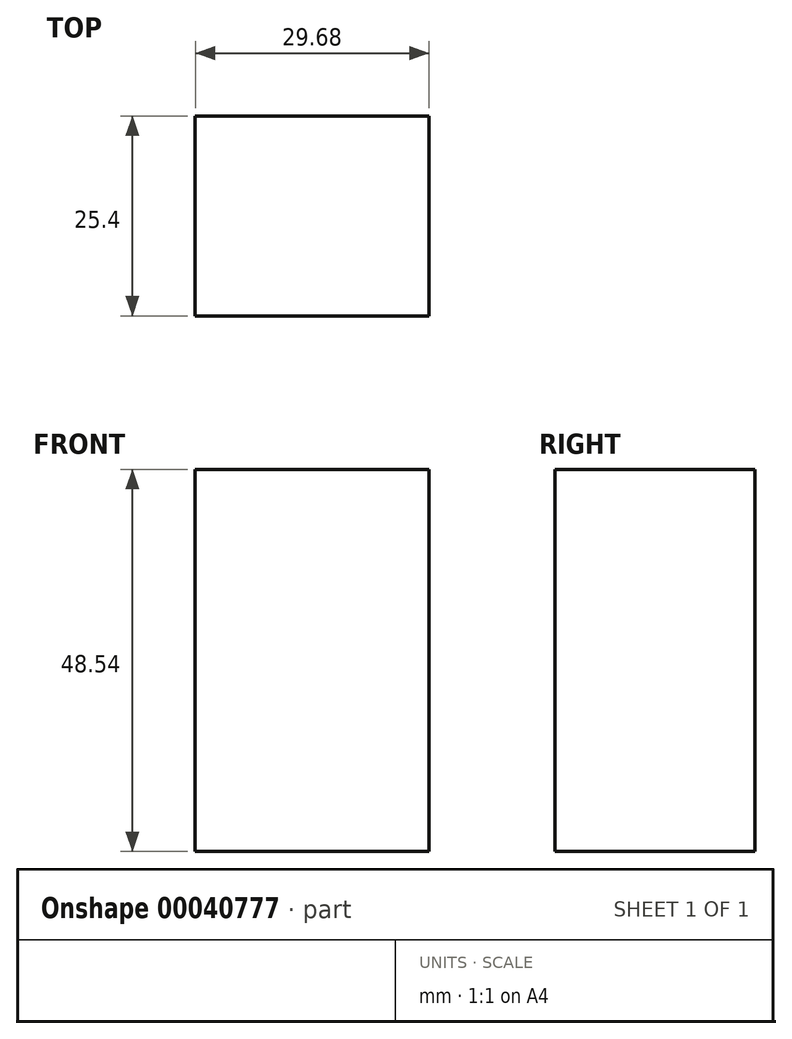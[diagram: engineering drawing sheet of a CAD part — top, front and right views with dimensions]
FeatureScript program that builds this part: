
annotation { "Feature Type Name" : "Feature", "Feature Type Description" : "" }
export const myFeature = defineFeature(function(context is Context, id is Id, definition is map)
    precondition{}
    {
        {
            var Q0;
            Q0=qCreatedBy(makeId("Front.planeOp"),FACE);
            var sketch = newSketch(context, id + "F0", { "sketchPlane" : qUnion([Q0])});
            skLineSegment(sketch, "E0.bottom", {"start": v(-59.37, 59.82) * mm, "end": v(-29.69, 59.82) * mm});
            skLineSegment(sketch, "E0.top", {"start": v(-59.37, 11.28) * mm, "end": v(-29.69, 11.28) * mm});
            skLineSegment(sketch, "E0.left", {"start": v(-59.37, 59.82) * mm, "end": v(-59.37, 11.28) * mm});
            skLineSegment(sketch, "E0.right", {"start": v(-29.69, 59.82) * mm, "end": v(-29.69, 11.28) * mm});
            skSolve(sketch);
        }
        {
            var Q0;
            Q0 = qSketchRegion(id + "F0", true);
            extrude(context, id + "F1", {"entities" : qUnion([Q0]), "depth" : 25.4 * mm});
        }
    });
